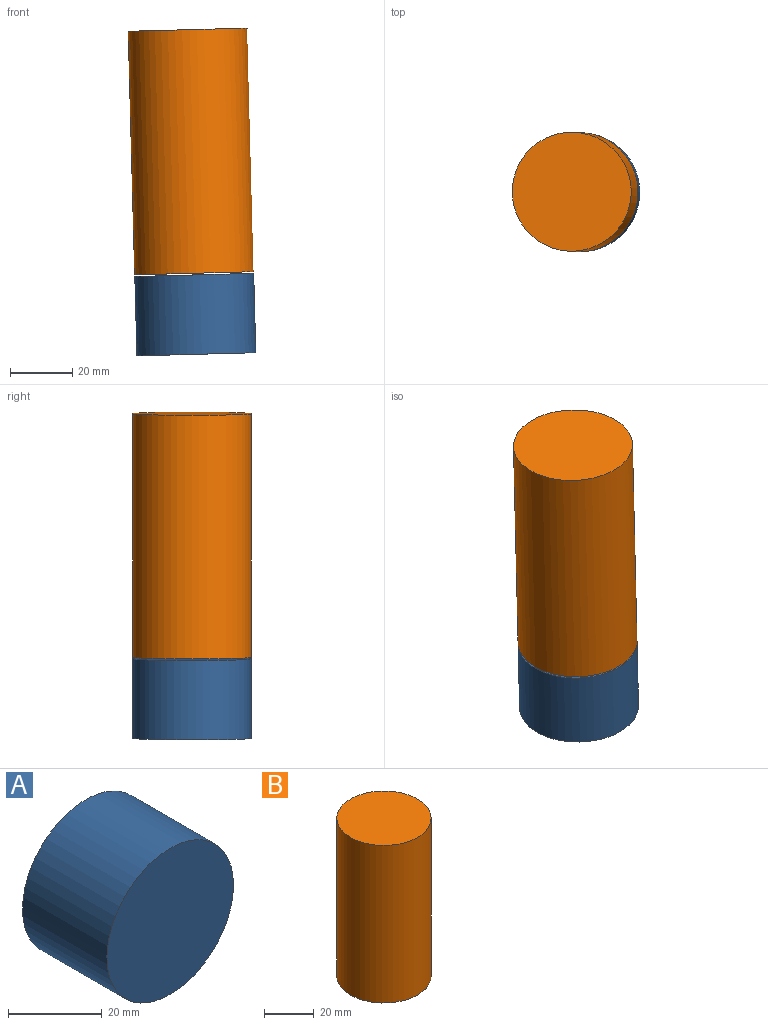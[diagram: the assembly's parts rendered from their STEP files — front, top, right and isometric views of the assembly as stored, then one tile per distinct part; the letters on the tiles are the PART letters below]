
ASSEMBLY  parts=2 mates=1
PART A: 3 faces, bbox 38.1x25.4x38.1 mm
  f0: cylinder r=19.05mm len=38.1mm, axis (0,1,0), area 3040.2mm2, adj f1,f2
  f1: plane 38.1x38.1mm, normal (0,-1,0), area 1140.1mm2, adj f0
  f2: plane 38.1x38.1mm, normal (0,1,0), area 1140.1mm2, adj f0
PART B: 3 faces, bbox 38.1x38.1x78 mm
  f0: plane 38.1x38.1mm, normal (0,0,-1), area 1140.1mm2, adj f2
  f1: plane 38.1x38.1mm, normal (0,0,1), area 1140.1mm2, adj f2
  f2: cylinder r=19.05mm len=77.99mm, axis (0,0,-1), area 9334.5mm2, adj f0,f1
PLACE A rot(axis=(-0.58,-0.58,0.57),120.9deg) t=(34.49,1.27,-24.27)mm
PLACE B rot(axis=(0,-1,0),1.5deg) t=(23.25,1.27,40.39)mm
MATE slider A.f0 <-> B.f2  axis (-0.03,0,1) through (33.81,1.27,1.12)mm
